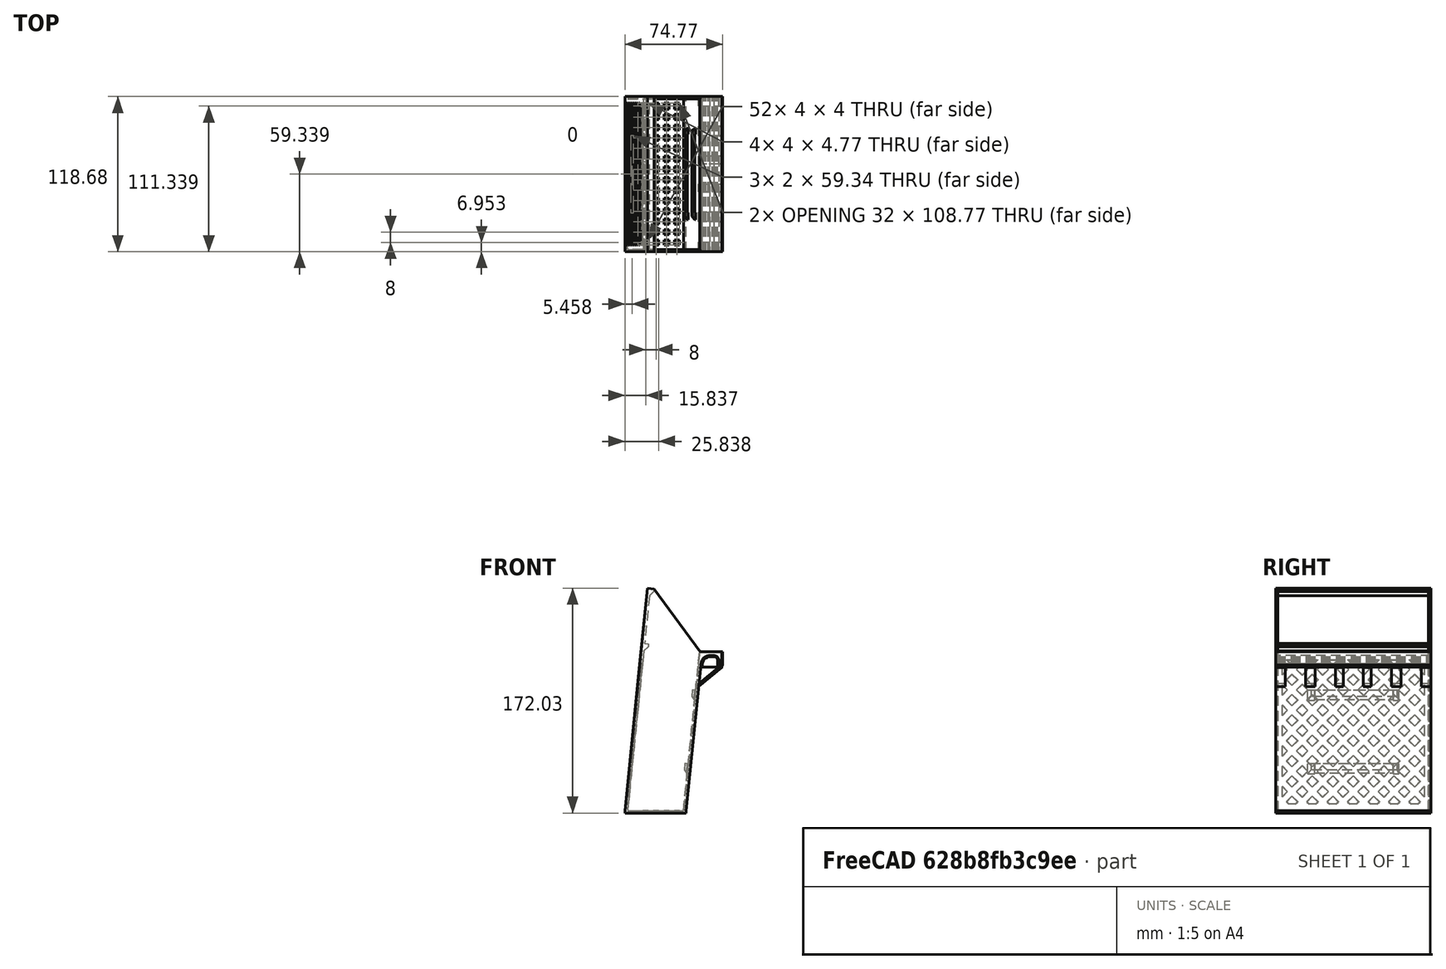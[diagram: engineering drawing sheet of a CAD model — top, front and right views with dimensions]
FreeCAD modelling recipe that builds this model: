
FCSTD DOCUMENT  (FreeCAD 0.18.4R)
Label: container-vertical
License: All rights reserved
LicenseURL: http://en.wikipedia.org/wiki/All_rights_reserved
objects: Part::Extrusion×38, Part::Part2DObjectPython×18, Part::Cut×17, Part::MultiFuse×16, Part::FeaturePython×11, Part::Feature×11, App::DocumentObjectGroup×4
note: 111 computed .brp shape members not serialized (recipe doc carries the construction recipe); baked Part::Feature solids carry a one-line shape summary decoded from their .brp

FEATURE [Part::MultiFuse] Fusion002003010002002002002002003010002003
FEATURE [Part::FeaturePython] Slice_child0  label="Slice.0"  # WARN: FeaturePython — macro-defined, semantics opaque (R4)
  FilterType = 1
  Invert = false
  OverrideMaxVal = 0
  WindowFrom = 80
  WindowTo = 100
  items = 0
FEATURE [App::DocumentObjectGroup] GrExplode_Slice  label="Exploded Slice"
  Group = -> [Slice_child0]
FEATURE [Part::Part2DObjectPython] Rectangle001  # Draft 2D object (typed FeaturePython)
  ChamferSize = 0
  Columns = 1
  FilletRadius = 0
  Height = 118.682
  Length = 8.45854
  MakeFace = true
  Placement = pos=(92.5503,-634.327,-183.654) rot=(0,0,1;0rad)
  Rows = 1
FEATURE [Part::Extrusion] Extrusion
  Base = -> Rectangle001
  Dir = (-3.858e-13,4.19e-14,-1.96794)
  DirMode = 0
  FaceMakerClass = Part::FaceMakerBullseye
  LengthFwd = 0
  LengthRev = 0
  Solid = true
  Symmetric = false
FEATURE [Part::Part2DObjectPython] Rectangle002  # Draft 2D object (typed FeaturePython)
  ChamferSize = 0
  Columns = 1
  FilletRadius = 0
  Height = 118.682
  Length = 38.3485
  MakeFace = true
  Placement = pos=(101.009,-634.327,-183.654) rot=(0,0,1;0rad)
  Rows = 1
FEATURE [Part::Extrusion] Extrusion001
  Base = -> Rectangle002
  Dir = (-3.858e-13,4.19e-14,-1.96794)
  DirMode = 0
  FaceMakerClass = Part::FaceMakerBullseye
  LengthFwd = 0
  LengthRev = 0
  Solid = true
  Symmetric = false
FEATURE [Part::Part2DObjectPython] Rectangle003  # Draft 2D object (typed FeaturePython)
  ChamferSize = 0
  Columns = 1
  FilletRadius = 0
  Height = 59.341
  Length = 2
  MakeFace = true
  Placement = pos=(97.0078,-604.656,-183.654) rot=(0,0,1;0rad)
  Rows = 1
  Support = -> [Extrusion]
FEATURE [Part::Extrusion] Extrusion002
  Base = -> Rectangle003
  Dir = (-2.0757e-12,2.249e-13,-10.6196)
  DirMode = 0
  FaceMakerClass = Part::FaceMakerBullseye
  LengthFwd = 0
  LengthRev = 0
  Solid = true
  Symmetric = false
FEATURE [Part::Cut] Cut
  Base = -> Extrusion
  Placement = pos=(-5.83e-13,160.755,3.382e-12) rot=(0,0,1;0rad)
  Tool = -> Extrusion002
FEATURE [Part::Part2DObjectPython] Rectangle004  # Draft 2D object (typed FeaturePython)
  ChamferSize = 0
  Columns = 1
  FilletRadius = 0
  Height = 31.3792
  Length = 108.772
  MakeFace = true
  Placement = pos=(103.008,-629.372,-185.622) rot=(0.707107,0.707107,0;3.14159rad)
  Rows = 1
FEATURE [Part::Extrusion] Extrusion003
  Base = -> Rectangle004
  Dir = (4.3131e-12,-4.721e-13,21.9833)
  DirMode = 0
  FaceMakerClass = Part::FaceMakerBullseye
  LengthFwd = 0
  LengthRev = 0
  Solid = true
  Symmetric = false
FEATURE [Part::Cut] Cut001
  Base = -> Extrusion001
  Placement = pos=(-5.969e-13,160.755,3.439e-12) rot=(0,0,1;0rad)
  Tool = -> Extrusion003
FEATURE [Part::Part2DObjectPython] Rectangle  # Draft 2D object (typed FeaturePython)
  ChamferSize = 0
  Columns = 1
  FilletRadius = 0
  Height = 4
  Length = 31.38
  MakeFace = true
  Placement = pos=(103.008,-464.617,-185.622) rot=(1,0,0;3.14159rad)
  Rows = 1
  Support = -> [Cut001]
FEATURE [Part::Extrusion] Extrusion004
  Base = -> Rectangle
  Dir = (3.858e-13,-4.19e-14,1.96794)
  DirMode = 0
  FaceMakerClass = Part::FaceMakerBullseye
  LengthFwd = 0
  LengthRev = 0
  Placement = pos=(0,4,8.5e-14) rot=(0,0,1;0rad)
  Solid = true
  Symmetric = false
FEATURE [Part::Extrusion] Extrusion005
  Base = -> Rectangle
  Dir = (3.858e-13,-4.19e-14,1.96794)
  DirMode = 0
  FaceMakerClass = Part::FaceMakerBullseye
  LengthFwd = 0
  LengthRev = 0
  Placement = pos=(0,12,2.56e-13) rot=(0,0,1;0rad)
  Solid = true
  Symmetric = false
FEATURE [Part::Extrusion] Extrusion006
  Base = -> Rectangle
  Dir = (3.858e-13,-4.19e-14,1.96794)
  DirMode = 0
  FaceMakerClass = Part::FaceMakerBullseye
  LengthFwd = 0
  LengthRev = 0
  Placement = pos=(0.000849151,20,4.26e-13) rot=(0,0,1;0rad)
  Solid = true
  Symmetric = false
FEATURE [Part::Extrusion] Extrusion007
  Base = -> Rectangle
  Dir = (3.858e-13,-4.19e-14,1.96794)
  DirMode = 0
  FaceMakerClass = Part::FaceMakerBullseye
  LengthFwd = 0
  LengthRev = 0
  Placement = pos=(0.000849151,28,5.97e-13) rot=(0,0,1;0rad)
  Solid = true
  Symmetric = false
FEATURE [Part::Extrusion] Extrusion008
  Base = -> Rectangle
  Dir = (3.858e-13,-4.19e-14,1.96794)
  DirMode = 0
  FaceMakerClass = Part::FaceMakerBullseye
  LengthFwd = 0
  LengthRev = 0
  Placement = pos=(0,36,7.671e-13) rot=(0,0,1;0rad)
  Solid = true
  Symmetric = false
FEATURE [Part::Extrusion] Extrusion009
  Base = -> Rectangle
  Dir = (3.858e-13,-4.19e-14,1.96794)
  DirMode = 0
  FaceMakerClass = Part::FaceMakerBullseye
  LengthFwd = 0
  LengthRev = 0
  Placement = pos=(0,44,9.381e-13) rot=(0,0,1;0rad)
  Solid = true
  Symmetric = false
FEATURE [Part::Extrusion] Extrusion010
  Base = -> Rectangle
  Dir = (3.858e-13,-4.19e-14,1.96794)
  DirMode = 0
  FaceMakerClass = Part::FaceMakerBullseye
  LengthFwd = 0
  LengthRev = 0
  Placement = pos=(0.000849151,52,1.1081e-12) rot=(0,0,1;0rad)
  Solid = true
  Symmetric = false
FEATURE [Part::Extrusion] Extrusion011
  Base = -> Rectangle
  Dir = (3.858e-13,-4.19e-14,1.96794)
  DirMode = 0
  FaceMakerClass = Part::FaceMakerBullseye
  LengthFwd = 0
  LengthRev = 0
  Placement = pos=(0.000849151,60,1.2791e-12) rot=(0,0,1;0rad)
  Solid = true
  Symmetric = false
FEATURE [Part::Extrusion] Extrusion012
  Base = -> Rectangle
  Dir = (3.858e-13,-4.19e-14,1.96794)
  DirMode = 0
  FaceMakerClass = Part::FaceMakerBullseye
  LengthFwd = 0
  LengthRev = 0
  Placement = pos=(0.000849151,92,1.9328e-12) rot=(0,0,1;0rad)
  Solid = true
  Symmetric = false
FEATURE [Part::Extrusion] Extrusion013
  Base = -> Rectangle
  Dir = (3.858e-13,-4.19e-14,1.96794)
  DirMode = 0
  FaceMakerClass = Part::FaceMakerBullseye
  LengthFwd = 0
  LengthRev = 0
  Placement = pos=(0.000849151,84,1.7618e-12) rot=(0,0,1;0rad)
  Solid = true
  Symmetric = false
FEATURE [Part::Extrusion] Extrusion014
  Base = -> Rectangle
  Dir = (3.858e-13,-4.19e-14,1.96794)
  DirMode = 0
  FaceMakerClass = Part::FaceMakerBullseye
  LengthFwd = 0
  LengthRev = 0
  Placement = pos=(0,76,1.5918e-12) rot=(0,0,1;0rad)
  Solid = true
  Symmetric = false
FEATURE [Part::Extrusion] Extrusion015
  Base = -> Rectangle
  Dir = (3.858e-13,-4.19e-14,1.96794)
  DirMode = 0
  FaceMakerClass = Part::FaceMakerBullseye
  LengthFwd = 0
  LengthRev = 0
  Placement = pos=(0,68,1.4208e-12) rot=(0,0,1;0rad)
  Solid = true
  Symmetric = false
FEATURE [Part::Extrusion] Extrusion016
  Base = -> Rectangle
  Dir = (3.858e-13,-4.19e-14,1.96794)
  DirMode = 0
  FaceMakerClass = Part::FaceMakerBullseye
  LengthFwd = 0
  LengthRev = 0
  Placement = pos=(0.000849151,100,2.046e-12) rot=(0,0,1;0rad)
  Solid = true
  Symmetric = false
FEATURE [Part::Part2DObjectPython] Rectangle005  # Draft 2D object (typed FeaturePython)
  ChamferSize = 0
  Columns = 1
  FilletRadius = 0
  Height = 108.772
  Length = 4
  MakeFace = true
  Placement = pos=(126.387,-359.845,-185.622) rot=(1,0,0;3.14159rad)
  Rows = 1
FEATURE [Part::Extrusion] Extrusion017 .. Extrusion020  x4 (patterned run collapsed; names and placements below)
  Base = -> Rectangle005
  Dir = (3.858e-13,-4.19e-14,1.96794)
  DirMode = 0
  FaceMakerClass = Part::FaceMakerBullseye
  LengthFwd = 0
  LengthRev = 0
  Solid = true
  Symmetric = false
  placements: 4 in arithmetic series — first pos=(0,0,0) rot=(0,0,1;0rad), step (-8,0,1.592e-12), last pos=(-24,0,4.776e-12) rot=(0,0,1;0rad)
FEATURE [Part::MultiFuse] Fusion
  Shapes = -> [Extrusion004,Extrusion016,Extrusion011,Extrusion010,Extrusion015,Extrusion008,Extrusion007,Extrusion005,Extrusion006,Extrusion019,Extrusion013,Extrusion012,Extrusion009,Extrusion014,Extrusion018,Extrusion017,Extrusion020]
FEATURE [Part::MultiFuse] Fusion002003010002002002002002003010002004
  Shapes = -> [Fusion,Cut001]
FEATURE [Part::MultiFuse] Fusion002003010002002002002002003010002005
  Shapes = -> [Cut,Fusion002003010002002002002002003010002004]
FEATURE [Part::Part2DObjectPython] Rectangle006  # Draft 2D object (typed FeaturePython)
  ChamferSize = 0
  Columns = 1
  FilletRadius = 0
  Height = 202
  Length = 109
  MakeFace = true
  Placement = pos=(41.7213,-313.231,-71.8326) rot=(1,0,0;3.14159rad)
  Rows = 1
  Support = -> [Slice_child0]
FEATURE [Part::FeaturePython] Slice  # WARN: FeaturePython — macro-defined, semantics opaque (R4)
  Base = -> Slice_child0
  Mode = 1
  Tolerance = 0
  Tools = -> [Rectangle006]
FEATURE [Part::FeaturePython] Slice_child0001  label="Slice.001"  # WARN: FeaturePython — macro-defined, semantics opaque (R4)
  Base = -> Slice
  FilterType = 1
  Invert = false
  OverrideMaxVal = 0
  WindowFrom = 80
  WindowTo = 100
  items = 0
FEATURE [Part::FeaturePython] Slice_child1  label="Slice.1"  # WARN: FeaturePython — macro-defined, semantics opaque (R4)
  Base = -> Slice
  FilterType = 1
  Invert = false
  OverrideMaxVal = 0
  WindowFrom = 80
  WindowTo = 100
  items = 1
FEATURE [App::DocumentObjectGroup] GrExplode_Slice001  label="Exploded Slice001"
  Group = -> [Slice_child1]
FEATURE [Part::Part2DObjectPython] Rectangle007  # Draft 2D object (typed FeaturePython)
  ChamferSize = 0
  Columns = 1
  FilletRadius = 0
  Height = 170
  Length = 168
  MakeFace = true
  Placement = pos=(135.348,-496.207,-203.402) rot=(0,-1,0;1.46952rad)
  Rows = 1
  Support = -> [Slice_child1]
FEATURE [Part::FeaturePython] Slice001  # WARN: FeaturePython — macro-defined, semantics opaque (R4)
  Base = -> Slice_child1
  Mode = 1
  Tolerance = 0
  Tools = -> [Rectangle007]
FEATURE [Part::FeaturePython] Slice001_child0  label="Slice001.0"  # WARN: FeaturePython — macro-defined, semantics opaque (R4)
  Base = -> Slice001
  FilterType = 1
  Invert = false
  OverrideMaxVal = 0
  WindowFrom = 80
  WindowTo = 100
  items = 0
FEATURE [Part::FeaturePython] Slice001_child2  label="Slice001.2"  # WARN: FeaturePython — macro-defined, semantics opaque (R4)
  Base = -> Slice001
  FilterType = 1
  Invert = false
  OverrideMaxVal = 0
  WindowFrom = 80
  WindowTo = 100
  items = 2
FEATURE [Part::FeaturePython] Slice001_child3  label="Slice001.3"  # WARN: FeaturePython — macro-defined, semantics opaque (R4)
  Base = -> Slice001
  FilterType = 1
  Invert = false
  OverrideMaxVal = 0
  WindowFrom = 80
  WindowTo = 100
  items = 3
FEATURE [Part::Feature] Fusion002003010002002002002002003010002006001  label="Fusion002003010002002002002002003010002007"
  shape: bbox 13.37 x 118.7 x 112 mm, 6 faces (baked)
FEATURE [Part::MultiFuse] Fusion002003010002002002002002003010002006002
  Shapes = -> [Fusion002003010002002002002002003010002006001,Slice001_child0]
FEATURE [Part::MultiFuse] Fusion002003010002002002002002003010002006003
  Shapes = -> [Fusion002003010002002002002002003010002005,Fusion002003010002002002002002003010002006002]
FEATURE [Part::MultiFuse] Fusion002003010002002002002002003010002006004
  Shapes = -> [Slice001_child2,Slice001_child3]
FEATURE [Part::MultiFuse] Fusion002003010002002002002002003010002006005
  Shapes = -> [Fusion002003010002002002002002003010002006004,Fusion002003010002002002002002003010002006003]
FEATURE [Part::MultiFuse] Fusion002003010002002002002002003010002006006
  Shapes = -> [Slice_child0001,Fusion002003010002002002002002003010002006005]
FEATURE [App::DocumentObjectGroup] GrExplode_Slice001001  label="Exploded Slice002"
  Group = -> [Fusion002003010002002002002002003010002006006]
FEATURE [Part::MultiFuse] Fusion002003010002002002002002003010002006007
  Shapes = -> [Fusion002003010002002002002002003010002006005,Slice_child0001]
FEATURE [Part::Part2DObjectPython] Rectangle009  # Draft 2D object (typed FeaturePython)
  ChamferSize = 0
  Columns = 1
  FilletRadius = 0
  Height = 30
  Length = 43.25
  MakeFace = true
  Placement = pos=(145.018,-369.89,-127.95) rot=(0.741992,0,0.670408;3.14159rad)
  Rows = 1
  Support = -> [Fusion002003010002002002002002003010002006007]
FEATURE [Part::Part2DObjectPython] Rectangle010  # Draft 2D object (typed FeaturePython)
  ChamferSize = 0
  Columns = 1
  FilletRadius = 0
  Height = 30
  Length = 43.25
  MakeFace = true
  Placement = pos=(145.018,-428.572,-127.95) rot=(0.741992,0,0.670408;3.14159rad)
  Rows = 1
  Support = -> [Fusion002003010002002002002002003010002006007]
FEATURE [Part::Extrusion] Extrusion021
  Base = -> Rectangle009
  Dir = (91.5642,-2.34597e-11,-9.3053)
  DirMode = 0
  FaceMakerClass = Part::FaceMakerBullseye
  LengthFwd = 0
  LengthRev = 0
  Solid = true
  Symmetric = false
FEATURE [Part::Extrusion] Extrusion022
  Base = -> Rectangle010
  Dir = (91.5642,-2.34587e-11,-9.3053)
  DirMode = 0
  FaceMakerClass = Part::FaceMakerBullseye
  LengthFwd = 0
  LengthRev = 0
  Solid = true
  Symmetric = false
FEATURE [Part::Cut] Cut002
  Base = -> Fusion002003010002002002002002003010002003
  Tool = -> Extrusion022
FEATURE [Part::Cut] Cut003
  Base = -> Cut002
  Tool = -> Extrusion021
FEATURE [Part::Part2DObjectPython] Rectangle011  # Draft 2D object (typed FeaturePython)
  ChamferSize = 0
  Columns = 1
  FilletRadius = 0
  Height = 30
  Length = 12.741
  MakeFace = true
  Placement = pos=(148.325,-428.572,-97.62) rot=(0.741992,0,0.670408;3.14159rad)
  Rows = 1
FEATURE [Part::Extrusion] Extrusion023
  Base = -> Rectangle011
  Dir = (15.8168,-4.0524e-12,-1.6074)
  DirMode = 0
  FaceMakerClass = Part::FaceMakerBullseye
  LengthFwd = 0
  LengthRev = 0
  Solid = true
  Symmetric = false
FEATURE [Part::Feature] DWire
FEATURE [Part::Part2DObjectPython] Wire  # Draft 2D object (typed FeaturePython)
  ChamferSize = 0
  Closed = true
  End = (164.141,-458.572,-99.2274)
  FilletRadius = 0
  Length = 49.013
  MakeFace = true
  Placement = pos=(149.613,-458.572,-84.9443) rot=(-0.538389,-0.595876,0.595876;4.12936rad)
  Points = (3) [(0,0,0),(0,15.8983,-5.68434e-14),(12.741,15.8983,-2.27374e-13)]
  Start = (149.613,-458.572,-84.9443)
  Subdivisions = 0
  Support = -> [Extrusion023]
FEATURE [Part::Extrusion] Extrusion024
  Base = -> Wire
  Dir = (-2.042e-13,67.7406,-1.70402e-10)
  DirMode = 0
  FaceMakerClass = Part::FaceMakerBullseye
  LengthFwd = 0
  LengthRev = 0
  Solid = true
  Symmetric = false
FEATURE [Part::Cut] Cut004
  Base = -> Extrusion023
  Placement = pos=(0.676604,2.23395e-11,8.86101) rot=(0,0,1;0rad)
  Tool = -> Extrusion024
FEATURE [Part::Cut] Cut005
  Base = -> Extrusion023
  Placement = pos=(0.676604,58.682,8.86101) rot=(0,0,1;0rad)
  Tool = -> Extrusion024
FEATURE [Part::Cut] Cut006
  Base = -> Cut003
  Tool = -> Cut004
FEATURE [Part::Cut] Cut007
  Base = -> Cut006
  Tool = -> Cut005
FEATURE [Part::Part2DObjectPython] Rectangle012  # Draft 2D object (typed FeaturePython)
  ChamferSize = 0
  Columns = 1
  FilletRadius = 0
  Height = 222
  Length = 138
  MakeFace = true
  Placement = pos=(101.133,-510.231,-73.8666) rot=(0,0,1;0rad)
  Rows = 1
  Support = -> [Cut007]
FEATURE [Part::FeaturePython] Slice002  # WARN: FeaturePython — macro-defined, semantics opaque (R4)
  Base = -> Cut007
  Mode = 1
  Tolerance = 0
  Tools = -> [Rectangle012]
FEATURE [Part::FeaturePython] Slice002_child0  label="Slice002.0"  # WARN: FeaturePython — macro-defined, semantics opaque (R4)
  Base = -> Slice002
  FilterType = 1
  Invert = false
  OverrideMaxVal = 0
  WindowFrom = 80
  WindowTo = 100
  items = 0
FEATURE [Part::FeaturePython] Slice002_child1  label="Slice002.1"  # WARN: FeaturePython — macro-defined, semantics opaque (R4)
  Base = -> Slice002
  FilterType = 1
  Invert = false
  OverrideMaxVal = 0
  WindowFrom = 80
  WindowTo = 100
  items = 1
FEATURE [Part::Part2DObjectPython] Wire001  # Draft 2D object (typed FeaturePython)
  ChamferSize = 0
  Closed = true
  End = (149.408,-473.572,-86.2219)
  FilletRadius = 0
  Length = 45.0098
  MakeFace = true
  Placement = pos=(151.389,-473.572,-73.8666) rot=(1,0,0;1.5708rad)
  Points = (3) [(0,0,0),(13.0441,-4.88853e-11,3.41061e-13),(-1.98083,-12.3554,-3.97904e-13)]
  Start = (151.389,-473.572,-73.8666)
  Subdivisions = 0
FEATURE [Part::Extrusion] Extrusion025
  Base = -> Wire001
  Dir = (1.47868e-11,231.564,8.9467e-12)
  DirMode = 0
  FaceMakerClass = Part::FaceMakerBullseye
  LengthFwd = 0
  LengthRev = 0
  Solid = true
  Symmetric = false
FEATURE [Part::Cut] Cut008
  Base = -> Slice002_child0
  Tool = -> Extrusion025
FEATURE [Part::Feature] Face
  Placement = pos=(0.20257,-486.273,50.5253) rot=(1,0,0;1.5708rad)
  shape: bbox 1.553e-06 x 118.7 x 11.21 mm, 1 faces, 0 solids (baked)
FEATURE [Part::Extrusion] Extrusion026
  Base = -> Face
  Dir = (0.40205,-3.3e-15,-7.5e-14)
  DirMode = 0
  FaceMakerClass = Part::FaceMakerBullseye
  LengthFwd = 0
  LengthRev = 0
  Solid = true
  Symmetric = false
FEATURE [Part::Feature] Face001
  shape: bbox 3e-07 x 118.7 x 0.4456 mm, 1 faces, 0 solids (baked)
FEATURE [Part::Extrusion] Extrusion027
  Base = -> Face001
  Dir = (0.250392,2.23e-14,-2.45e-14)
  DirMode = 0
  FaceMakerClass = Part::FaceMakerBullseye
  LengthFwd = 0
  LengthRev = 0
  Solid = true
  Symmetric = false
FEATURE [Part::Part2DObjectPython] Wire002  # Draft 2D object (typed FeaturePython)
  ChamferSize = 0
  Closed = true
  End = (166.924,-473.572,-74.3122)
  FilletRadius = 0
  Length = 1.2071
  MakeFace = true
  Placement = pos=(166.924,-473.572,-73.8666) rot=(1,0,0;1.5708rad)
  Points = (3) [(0,0,0),(-0.250392,-0.445588,0),(-5.68434e-14,-0.445588,-5.68434e-14)]
  Start = (166.924,-473.572,-73.8666)
  Subdivisions = 0
FEATURE [Part::Extrusion] Extrusion028
  Base = -> Wire002
  Dir = (-3.8745e-12,125.973,9.2872e-12)
  DirMode = 0
  FaceMakerClass = Part::FaceMakerBullseye
  LengthFwd = 0
  LengthRev = 0
  Solid = true
  Symmetric = false
FEATURE [Part::Cut] Cut009
  Base = -> Extrusion027
  Tool = -> Extrusion028
FEATURE [Part::MultiFuse] Fusion002003010002002002002002003010002006008
  Shapes = -> [Cut008,Cut009]
FEATURE [Part::MultiFuse] Fusion002003010002002002002002003010002006009
  Shapes = -> [Fusion002003010002002002002002003010002006007,Extrusion026]
FEATURE [Part::Part2DObjectPython] Rectangle013  # Draft 2D object (typed FeaturePython)
  ChamferSize = 0
  Columns = 1
  FilletRadius = 0
  Height = 30.6628
  Length = 16
  MakeFace = true
  Placement = pos=(149.001,-427.91,-88.759) rot=(0.741992,0,0.670408;3.14159rad)
  Rows = 1
  Support = -> [Fusion002003010002002002002002003010002006009]
FEATURE [Part::Extrusion] Extrusion029
  Base = -> Rectangle013
  Dir = (42.5816,-1.09099e-11,-4.3274)
  DirMode = 0
  FaceMakerClass = Part::FaceMakerBullseye
  LengthFwd = 0
  LengthRev = 0
  Solid = true
  Symmetric = false
FEATURE [Part::Feature] Face004
  shape: bbox 42.58 x 30.66 x 4.327 mm, 1 faces, 0 solids (baked)
FEATURE [Part::Extrusion] Extrusion031
  Base = -> Face004
  Dir = (0.101898,2.5275e-12,1.00267)
  DirMode = 0
  FaceMakerClass = Part::FaceMakerBullseye
  LengthFwd = 0
  LengthRev = 0
  Solid = true
  Symmetric = false
FEATURE [Part::MultiFuse] Fusion002003010002002002002002003010002006010
  Placement = pos=(1.30171e-11,58.0192,7.85008e-11) rot=(0,0,1;0rad)
  Shapes = -> [Extrusion031,Extrusion029]
FEATURE [Part::MultiFuse] Fusion002003010002002002002002003010002006011
  Shapes = -> [Extrusion031,Extrusion029]
FEATURE [Part::Cut] Cut010
  Base = -> Fusion002003010002002002002002003010002006008
  Tool = -> Fusion002003010002002002002002003010002006010
FEATURE [Part::Cut] Cut011
  Base = -> Cut010
  Tool = -> Fusion002003010002002002002002003010002006011
FEATURE [Part::Feature] Fusion002003010002002002002002003010002006012001  label="Fusion002003010002002002002002003010002006013"
  shape: bbox 44.3 x 15.33 x 21.27 mm, 6 faces (baked)
FEATURE [Part::Feature] Face009
  shape: bbox 44.3 x 4.243e-07 x 21.27 mm, 1 faces, 0 solids (baked)
FEATURE [Part::Extrusion] Extrusion034
  Base = -> Face009
  Dir = (-2.2e-15,7.66571,-1.93058e-11)
  DirMode = 0
  FaceMakerClass = Part::FaceMakerBullseye
  LengthFwd = 0
  LengthRev = 0
  Placement = pos=(6.5086e-12,52.0067,-1.87157e-11) rot=(0,0,1;0rad)
  Solid = true
  Symmetric = false
FEATURE [Part::Cut] Cut012
  Base = -> Cut011
  Tool = -> Fusion002003010002002002002002003010002006012001
FEATURE [Part::Extrusion] Extrusion035
  Base = -> Face009
  Dir = (-2.2e-15,7.66571,-1.93058e-11)
  DirMode = 0
  FaceMakerClass = Part::FaceMakerBullseye
  LengthFwd = 0
  LengthRev = 0
  Placement = pos=(-6.509e-12,-44.341,-6.11e-13) rot=(0,0,1;0rad)
  Solid = true
  Symmetric = false
FEATURE [Part::Cut] Cut013
  Base = -> Cut012
  Tool = -> Extrusion035
FEATURE [Part::Cut] Cut014
  Base = -> Cut013
  Tool = -> Extrusion034
FEATURE [App::DocumentObjectGroup] GrExplode_Slice002  label="Exploded Slice003"
  Group = -> [Slice002_child1,Cut014]
FEATURE [Part::Feature] Cut014001  label="Cut015"
  shape: bbox 17.92 x 118.7 x 14.89 mm, 28 faces, 4 solids (baked)
FEATURE [Part::Feature] Face010
  shape: bbox 17.92 x 5.243e-07 x 14.89 mm, 1 faces, 0 solids (baked)
FEATURE [Part::Extrusion] Extrusion036
  Base = -> Face010
  Dir = (-5.73e-13,7.33429,1.3247e-12)
  DirMode = 0
  FaceMakerClass = Part::FaceMakerBullseye
  LengthFwd = 0
  LengthRev = 0
  Placement = pos=(-2.842e-13,22.8314,-4.76632e-11) rot=(0,0,1;0rad)
  Solid = true
  Symmetric = false
FEATURE [Part::Extrusion] Extrusion037
  Base = -> Face010
  Dir = (-5.73e-13,7.33429,1.3247e-12)
  DirMode = 0
  FaceMakerClass = Part::FaceMakerBullseye
  LengthFwd = 0
  LengthRev = 0
  Placement = pos=(-7.9581e-12,88.5163,3.23581e-11) rot=(0,0,1;0rad)
  Solid = true
  Symmetric = false
FEATURE [Part::MultiFuse] Fusion002003010002002002002002003010002006012002
  Shapes = -> [Cut014001,Extrusion036,Extrusion037]
FEATURE [Part::Feature] Face012
  Placement = pos=(0.60462,-486.273,50.5253) rot=(1,0,0;1.5708rad)
  shape: bbox 1.553e-06 x 118.7 x 11.21 mm, 1 faces, 0 solids (baked)
FEATURE [Part::Extrusion] Extrusion038
  Base = -> Face012
  Dir = (0.392283,-3.3e-15,-7.31e-14)
  DirMode = 0
  FaceMakerClass = Part::FaceMakerBullseye
  LengthFwd = 0
  LengthRev = 0
  Solid = true
  Symmetric = false
FEATURE [Part::MultiFuse] Fusion002003010002002002002002003010002006012003
  Shapes = -> [Extrusion038,Fusion002003010002002002002002003010002006009]
FEATURE [Part::Part2DObjectPython] Rectangle014  # Draft 2D object (typed FeaturePython)
  ChamferSize = 0
  Columns = 1
  FilletRadius = 0
  Height = 0.445588
  Length = 0.250392
  MakeFace = true
  Placement = pos=(166.673,-473.572,-74.3122) rot=(1,0,0;1.5708rad)
  Rows = 1
FEATURE [Part::Extrusion] Extrusion039
  Base = -> Rectangle014
  Dir = (2.81674e-11,143.52,-7.728e-12)
  DirMode = 0
  FaceMakerClass = Part::FaceMakerBullseye
  LengthFwd = 0
  LengthRev = 0
  Solid = true
  Symmetric = false
FEATURE [Part::Cut] Cut014002
  Base = -> Fusion002003010002002002002002003010002006012002
  Tool = -> Extrusion039
FEATURE [Part::Part2DObjectPython] Wire003  # Draft 2D object (typed FeaturePython)
  ChamferSize = 0
  Closed = true
  End = (167.316,-473.572,-73.4645)
  FilletRadius = 0
  Length = 3.09866
  MakeFace = true
  Placement = pos=(166.522,-473.572,-73.4645) rot=(-0.57735,0.57735,-0.57735;2.0944rad)
  Points = (3) [(0,0,0),(-3.41061e-13,-1.01525,0.794333),(5.68434e-14,5.68434e-14,0.794333)]
  Start = (166.522,-473.572,-73.4645)
  Subdivisions = 0
  Support = -> [Fusion002003010002002002002002003010002006012003]
FEATURE [Part::Extrusion] Extrusion040
  Base = -> Wire003
  Dir = (-2.1416e-12,125.72,-3.5385e-11)
  DirMode = 0
  FaceMakerClass = Part::FaceMakerBullseye
  LengthFwd = 0
  LengthRev = 0
  Solid = true
  Symmetric = false
FEATURE [Part::Cut] Cut014003
  Base = -> Fusion002003010002002002002002003010002006012003
  Tool = -> Extrusion040
FEATURE [Part::Feature] Cut014003001  label="Cut014004"
  shape: bbox 74.77 x 118.7 x 172 mm, 711 faces (baked)
